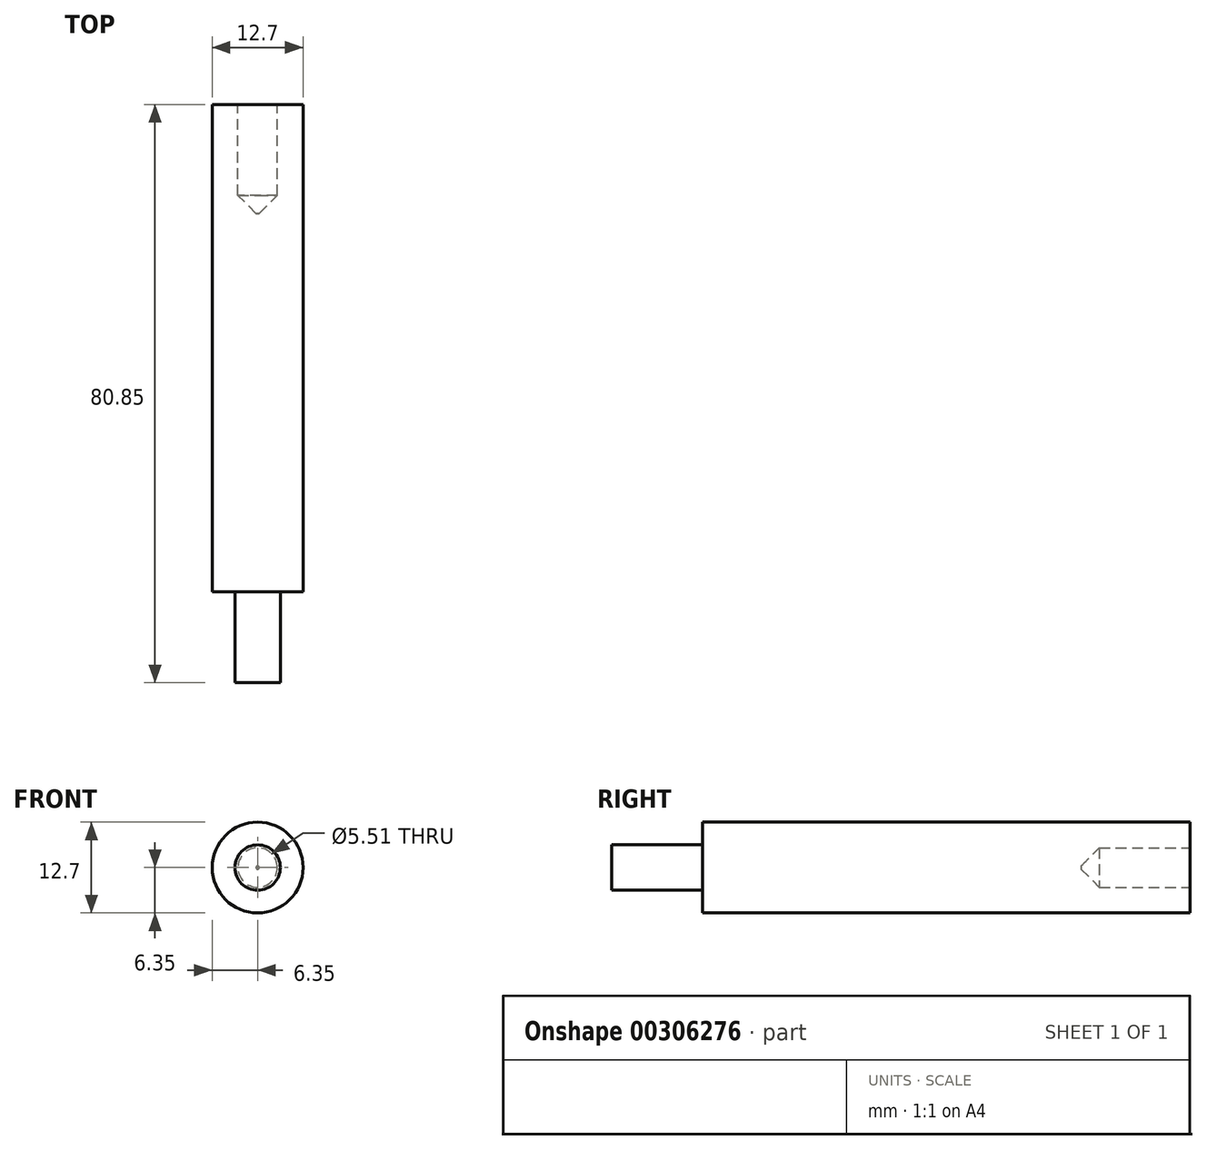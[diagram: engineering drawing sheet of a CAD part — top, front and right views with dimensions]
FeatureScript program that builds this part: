
annotation { "Feature Type Name" : "Feature", "Feature Type Description" : "" }
export const myFeature = defineFeature(function(context is Context, id is Id, definition is map)
    precondition{}
    {
        {
            var Q0;
            Q0=qCreatedBy(makeId("Front.planeOp"),FACE);
            var sketch = newSketch(context, id + "F0", { "sketchPlane" : qUnion([Q0])});
            skCircle(sketch, "E0", {"center": v(0, 0) * mm, "radius": 6.35 * mm});
            skSolve(sketch);
        }
        {
            var Q0;
            Q0 = qSketchRegion(id + "F0", true);
            extrude(context, id + "F1", {"entities" : qUnion([Q0]), "depth" : 80.85 * mm});
        }
        {
            var Q0;
            Q0=makeQuery(id+"F1.opExtrude","CAP_FACE",FACE,{"disambiguationData":[OSD([sQuery(id+"F0.wireOp",EDGE,"E0")])],"isStart":false});
            var sketch = newSketch(context, id + "F2", { "sketchPlane" : qUnion([Q0])});
            skCircle(sketch, "E1", {"center": v(0, 0) * mm, "radius": 6.35 * mm});
            skCircle(sketch, "E2", {"center": v(0, 0) * mm, "radius": 3.18 * mm});
            skSolve(sketch);
        }
        {
            var Q0;
            Q0 = qSketchRegion(id + "F2", true);
            extrude(context, id + "F3", {"entities" : qUnion([Q0]), "operationType" : NewBodyOperationType.REMOVE, "oppositeDirection" : true, "depth" : 12.7 * mm});
        }
        {
            var Q0;
            Q0=makeQuery(id+"F1.opExtrude","CAP_FACE",FACE,{"disambiguationData":[OSD([sQuery(id+"F0.wireOp",EDGE,"E0")])],"isStart":true});
            var sketch = newSketch(context, id + "F4", { "sketchPlane" : qUnion([Q0])});
            skCircle(sketch, "E3", {"center": v(0, 0) * mm, "radius": 2.76 * mm});
            skSolve(sketch);
        }
        {
            var Q0;
            Q0 = qSketchRegion(id + "F4", true);
            extrude(context, id + "F5", {"entities" : qUnion([Q0]), "operationType" : NewBodyOperationType.REMOVE, "oppositeDirection" : true, "depth" : 12.7 * mm});
        }
        {
            var Q0;
            Q0=makeQuery(id+"F5.boolean.opBoolean","COPY",FACE,{"derivedFrom":makeQuery(id+"F5.opExtrude","CAP_FACE",FACE,{"disambiguationData":[OSD([sQuery(id+"F4.wireOp",EDGE,"E3")])],"isStart":false})});
            var sketch = newSketch(context, id + "F6", { "sketchPlane" : qUnion([Q0])});
            skCircle(sketch, "E4", {"center": v(0, 0) * mm, "radius": 2.76 * mm});
            skSolve(sketch);
        }
        {
            var Q0;
            Q0 = qSketchRegion(id + "F6", true);
            extrude(context, id + "F7", {"entities" : qUnion([Q0]), "operationType" : NewBodyOperationType.REMOVE, "oppositeDirection" : true, "depth" : 2.54 * mm, "hasDraft" : true, "draftAngle" : 45 * degree, "draftPullDirection" : true});
        }
    });
